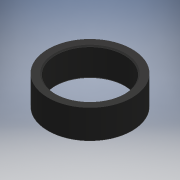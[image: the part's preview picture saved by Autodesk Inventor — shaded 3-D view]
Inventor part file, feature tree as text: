
AUTODESK INVENTOR PART (.ipt)
format: ipt  version: 2018 (Build 220112000, 112)  size: 107,520 bytes
history: native  units: mm
features: extrude x1, chamfer x1, sketch x1
ambient origin geometry x8: Origin, YZ Plane, XZ Plane, XY Plane, X Axis, Y Axis, Z Axis, Center Point
bodies: Solido1 (feature_tree)
feature tree (3):
  extrude  "Estrusione1"  Depth=28.5mm
  chamfer  "Smusso1"  Distance=35.0mm
  sketch  "Schizzo1"
